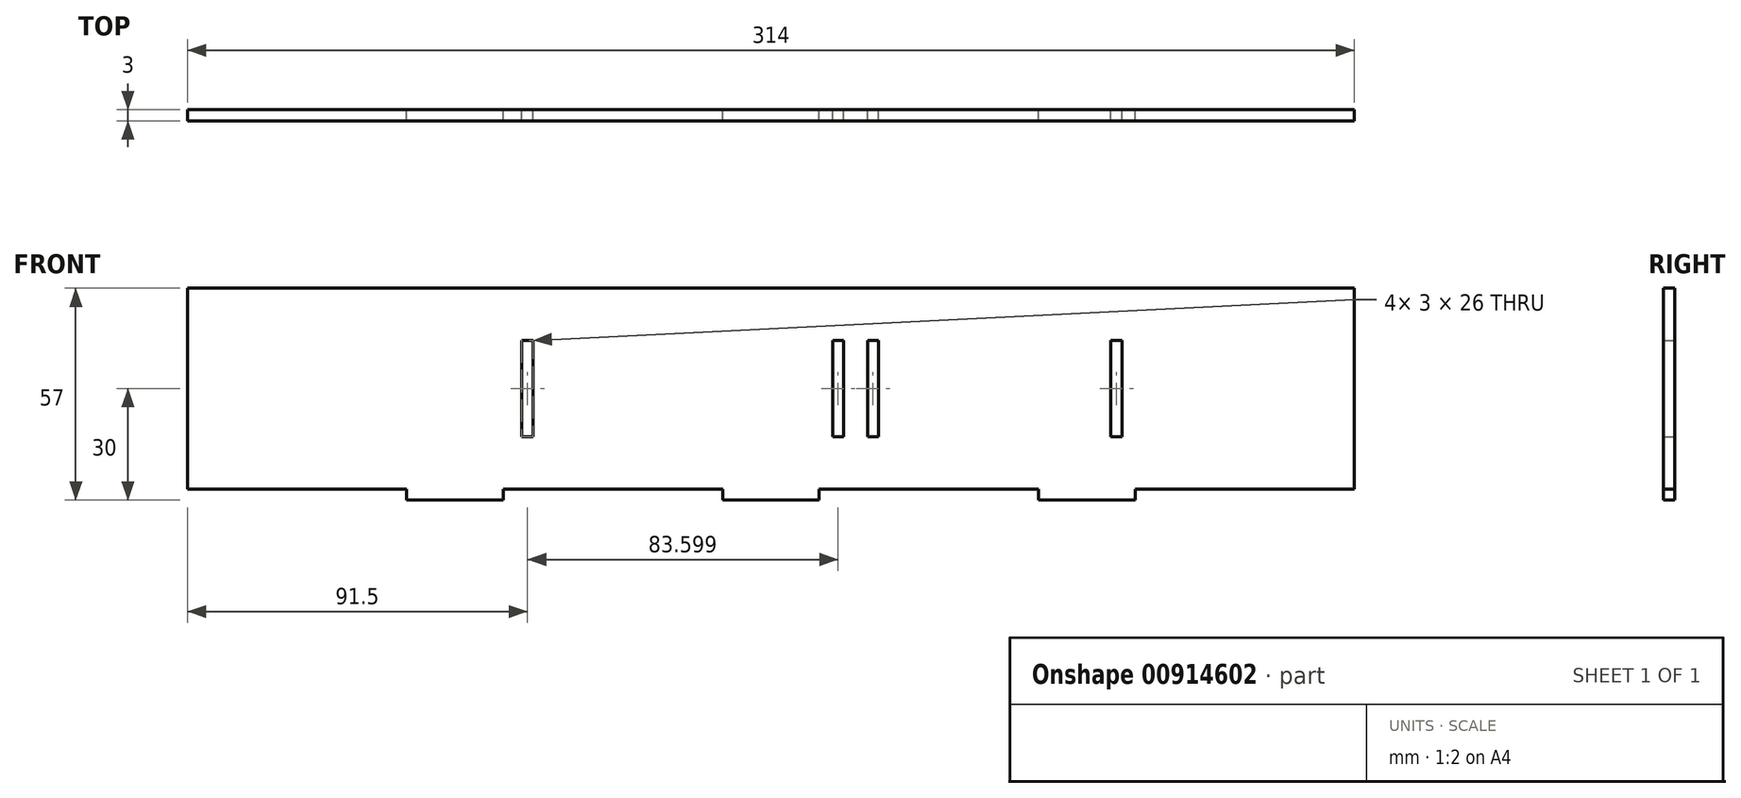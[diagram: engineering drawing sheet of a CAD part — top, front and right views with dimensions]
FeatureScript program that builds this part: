
annotation { "Feature Type Name" : "Feature", "Feature Type Description" : "" }
export const myFeature = defineFeature(function(context is Context, id is Id, definition is map)
    precondition{}
    {
        {
            var Q0;
            Q0=qCreatedBy(makeId("Front.planeOp"),FACE);
            var sketch = newSketch(context, id + "F0", { "sketchPlane" : qUnion([Q0])});
            skLineSegment(sketch, "E0.bottom", {"start": v(98, -28.5) * mm, "end": v(72, -28.5) * mm});
            skLineSegment(sketch, "E0.top", {"start": v(157, 28.5) * mm, "end": v(-157, 28.5) * mm});
            skLineSegment(sketch, "E0.left", {"start": v(157, -25.5) * mm, "end": v(157, 28.5) * mm});
            skLineSegment(sketch, "E0.right", {"start": v(-157, -25.5) * mm, "end": v(-157, 28.5) * mm});
            skPoint(sketch, "E0.middle", {"position": v(0, 0) * mm});
            skLineSegment(sketch, "E1", {"start": v(-157, -25.5) * mm, "end": v(-98, -25.5) * mm});
            skLineSegment(sketch, "E2", {"start": v(-98, -25.5) * mm, "end": v(-98, -28.5) * mm});
            skLineSegment(sketch, "E3", {"start": v(-72, -25.5) * mm, "end": v(-72, -28.5) * mm});
            skLineSegment(sketch, "E4", {"start": v(-13, -25.5) * mm, "end": v(-13, -28.5) * mm});
            skLineSegment(sketch, "E5", {"start": v(13, -25.5) * mm, "end": v(13, -28.5) * mm});
            skLineSegment(sketch, "E6", {"start": v(72, -25.5) * mm, "end": v(72, -28.5) * mm});
            skLineSegment(sketch, "E7", {"start": v(98, -25.5) * mm, "end": v(98, -28.5) * mm});
            skPoint(sketch, "E8.orphan", {"position": v(-157, -28.5) * mm});
            skLineSegment(sketch, "E9.trimOffspring", {"start": v(-72, -25.5) * mm, "end": v(-13, -25.5) * mm});
            skLineSegment(sketch, "E10.trimOffspring", {"start": v(-72, -28.5) * mm, "end": v(-98, -28.5) * mm});
            skLineSegment(sketch, "E11.trimOffspring", {"start": v(13, -25.5) * mm, "end": v(72, -25.5) * mm});
            skLineSegment(sketch, "E12.trimOffspring", {"start": v(13, -28.5) * mm, "end": v(-13, -28.5) * mm});
            skLineSegment(sketch, "E13.trimOffspring", {"start": v(98, -25.5) * mm, "end": v(157, -25.5) * mm});
            skPoint(sketch, "E14.orphan", {"position": v(157, -28.5) * mm});
            skLineSegment(sketch, "E15", {"start": v(19.6, 14.5) * mm, "end": v(19.6, -11.5) * mm});
            skLineSegment(sketch, "E16", {"start": v(16.6, 14.5) * mm, "end": v(16.6, -11.5) * mm});
            skLineSegment(sketch, "E17", {"start": v(16.6, 14.5) * mm, "end": v(19.6, 14.5) * mm});
            skLineSegment(sketch, "E18", {"start": v(16.6, -11.5) * mm, "end": v(19.6, -11.5) * mm});
            skLineSegment(sketch, "E19", {"start": v(-67, 14.5) * mm, "end": v(-67, -11.5) * mm});
            skLineSegment(sketch, "E20", {"start": v(-64, 14.5) * mm, "end": v(-64, -11.5) * mm});
            skLineSegment(sketch, "E21", {"start": v(-64, 14.5) * mm, "end": v(-67, 14.5) * mm});
            skLineSegment(sketch, "E22", {"start": v(-67, -11.5) * mm, "end": v(-64, -11.5) * mm});
            skLineSegment(sketch, "E23", {"start": v(26, 14.5) * mm, "end": v(26, -11.5) * mm});
            skLineSegment(sketch, "E24", {"start": v(29, 14.5) * mm, "end": v(29, -11.5) * mm});
            skLineSegment(sketch, "E25", {"start": v(26, 14.5) * mm, "end": v(29, 14.5) * mm});
            skLineSegment(sketch, "E26", {"start": v(26, -11.5) * mm, "end": v(29, -11.5) * mm});
            skLineSegment(sketch, "E27", {"start": v(91.5, 14.5) * mm, "end": v(91.5, -11.5) * mm});
            skLineSegment(sketch, "E28", {"start": v(94.5, 14.5) * mm, "end": v(94.5, -11.5) * mm});
            skLineSegment(sketch, "E29", {"start": v(91.5, 14.5) * mm, "end": v(94.5, 14.5) * mm});
            skLineSegment(sketch, "E30", {"start": v(91.5, -11.5) * mm, "end": v(94.5, -11.5) * mm});
            skPoint(sketch, "E30.startSnap0", {"position": v(91.5, 1.5) * mm});
            skPoint(sketch, "E31.orphan", {"position": v(91.5, 28.5) * mm});
            skPoint(sketch, "E32.orphan", {"position": v(94.5, -25.5) * mm});
            skPoint(sketch, "E33.orphan", {"position": v(91.5, -25.5) * mm});
            skSolve(sketch);
        }
        {
            var Q0;
            Q0 = qSketchRegion(id + "F0", true);
            extrude(context, id + "F1", {"entities" : qUnion([Q0]), "depth" : 3 * mm, "offsetDistance" : 25 * mm});
        }
    });
